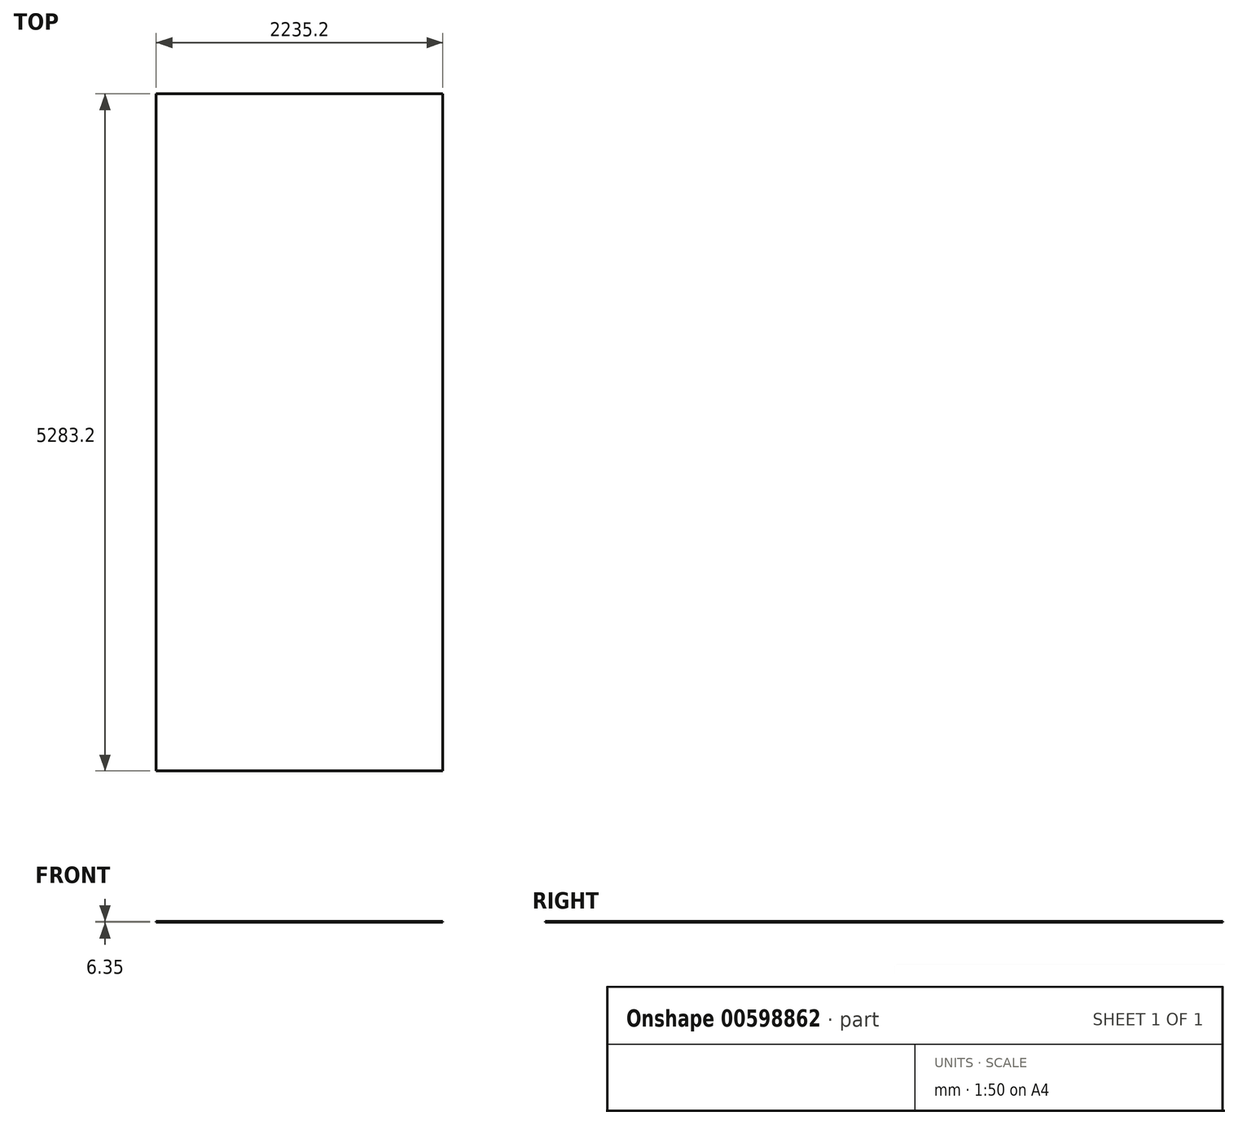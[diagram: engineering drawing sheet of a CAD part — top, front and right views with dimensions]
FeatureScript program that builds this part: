
annotation { "Feature Type Name" : "Feature", "Feature Type Description" : "" }
export const myFeature = defineFeature(function(context is Context, id is Id, definition is map)
    precondition{}
    {
        {
            var Q0;
            Q0=qCreatedBy(makeId("Top.planeOp"),FACE);
            var sketch = newSketch(context, id + "F0", { "sketchPlane" : qUnion([Q0])});
            skLineSegment(sketch, "E0.bottom", {"start": v(1062.2, -1046.6) * mm, "end": v(-1173, -1046.6) * mm});
            skLineSegment(sketch, "E0.top", {"start": v(1062.2, 4236.6) * mm, "end": v(-1173, 4236.6) * mm});
            skLineSegment(sketch, "E0.left", {"start": v(1062.2, -1046.6) * mm, "end": v(1062.2, 4236.6) * mm});
            skLineSegment(sketch, "E0.right", {"start": v(-1173, -1046.6) * mm, "end": v(-1173, 4236.6) * mm});
            skPoint(sketch, "E0.middle", {"position": v(-55.4, 1595) * mm});
            skSolve(sketch);
        }
        {
            var Q0;
            Q0 = qSketchRegion(id + "F0", true);
            extrude(context, id + "F1", {"entities" : qUnion([Q0]), "depth" : 6.35 * mm, "offsetDistance" : 25.4 * mm});
        }
    });
